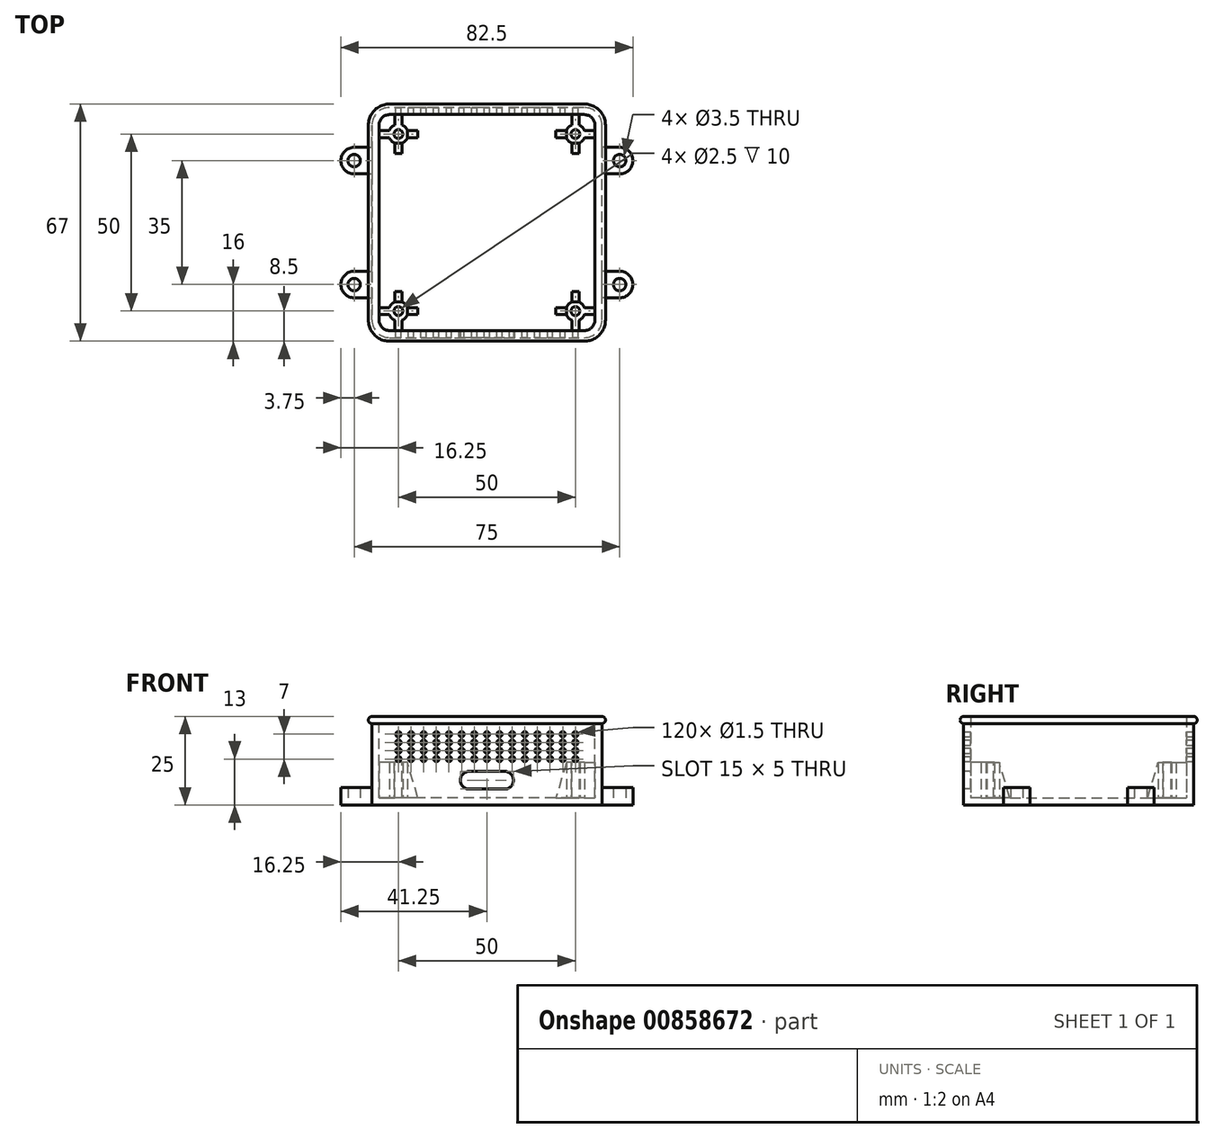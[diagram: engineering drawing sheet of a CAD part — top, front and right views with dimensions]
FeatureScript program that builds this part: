
annotation { "Feature Type Name" : "Feature", "Feature Type Description" : "" }
export const myFeature = defineFeature(function(context is Context, id is Id, definition is map)
    precondition{}
    {
        {
            var Q0;
            Q0=qCreatedBy(makeId("Top.planeOp"),FACE);
            var sketch = newSketch(context, id + "F0", { "sketchPlane" : qUnion([Q0])});
            skLineSegment(sketch, "E0.bottom", {"start": v(27.5, -32.5) * mm, "end": v(-27.5, -32.5) * mm});
            skLineSegment(sketch, "E0.top", {"start": v(27.5, 32.5) * mm, "end": v(-27.5, 32.5) * mm});
            skLineSegment(sketch, "E0.left", {"start": v(32.5, -27.5) * mm, "end": v(32.5, 27.5) * mm});
            skLineSegment(sketch, "E0.right", {"start": v(-32.5, -27.5) * mm, "end": v(-32.5, 27.5) * mm});
            skPoint(sketch, "E0.middle", {"position": v(0, 0) * mm});
            skPoint(sketch, "E1.visualSharp", {"position": v(-32.5, 32.5) * mm});
            skArc(sketch, "E1.filletArc", {"start": v(-27.5, 32.5) * mm, "mid": v(-31.04, 31.04) * mm, "end": v(-32.5, 27.5) * mm});
            skPoint(sketch, "E2.visualSharp", {"position": v(32.5, 32.5) * mm});
            skArc(sketch, "E2.filletArc", {"start": v(32.5, 27.5) * mm, "mid": v(31.04, 31.04) * mm, "end": v(27.5, 32.5) * mm});
            skPoint(sketch, "E3.visualSharp", {"position": v(32.5, -32.5) * mm});
            skArc(sketch, "E3.filletArc", {"start": v(27.5, -32.5) * mm, "mid": v(31.04, -31.04) * mm, "end": v(32.5, -27.5) * mm});
            skPoint(sketch, "E4.visualSharp", {"position": v(-32.5, -32.5) * mm});
            skArc(sketch, "E4.filletArc", {"start": v(-32.5, -27.5) * mm, "mid": v(-31.04, -31.04) * mm, "end": v(-27.5, -32.5) * mm});
            skSolve(sketch);
        }
        {
            var Q0;
            Q0 = qSketchRegion(id + "F0", true);
            extrude(context, id + "F1", {"entities" : qUnion([Q0]), "depth" : 25 * mm, "offsetDistance" : 25 * mm});
        }
        {
            var Q0;
            Q0=makeQuery(id+"F1.opExtrude","CAP_FACE",FACE,{"disambiguationData":[OSD([sQuery(id+"F0.wireOp",EDGE,"E0.bottom"),sQuery(id+"F0.wireOp",EDGE,"E0.top"),sQuery(id+"F0.wireOp",EDGE,"E0.left"),sQuery(id+"F0.wireOp",EDGE,"E0.right")])],"isStart":false});
            shell(context, id + "F2", {"entities" : qUnion([Q0]), "thickness" : 2 * mm});
        }
        {
            var Q0;
            Q0=qCreatedBy(makeId("Top.planeOp"),FACE);
            var sketch = newSketch(context, id + "F3", { "sketchPlane" : qUnion([Q0])});
            skLineSegment(sketch, "E5.bottom", {"start": v(-37.5, 21.25) * mm, "end": v(-32.5, 21.25) * mm});
            skLineSegment(sketch, "E5.top", {"start": v(-37.5, 13.75) * mm, "end": v(-32.5, 13.75) * mm});
            skLineSegment(sketch, "E5.right", {"start": v(-32.5, 21.25) * mm, "end": v(-32.5, 13.75) * mm});
            skArc(sketch, "E6", {"start": v(-37.5, 21.25) * mm, "mid": v(-41.25, 17.5) * mm, "end": v(-37.5, 13.75) * mm});
            skCircle(sketch, "E7", {"center": v(-37.5, 17.5) * mm, "radius": 1.75 * mm});
            skArc(sketch, "E8.MirrorCS", {"start": v(37.5, 21.25) * mm, "mid": v(41.25, 17.5) * mm, "end": v(37.5, 13.75) * mm});
            skCircle(sketch, "E9.MirrorC", {"center": v(37.5, 17.5) * mm, "radius": 1.75 * mm});
            skLineSegment(sketch, "E10.MirrorCS", {"start": v(32.5, 21.25) * mm, "end": v(32.5, 13.75) * mm});
            skLineSegment(sketch, "E11.MirrorCS", {"start": v(37.5, 13.75) * mm, "end": v(32.5, 13.75) * mm});
            skLineSegment(sketch, "E12.MirrorCS", {"start": v(37.5, 21.25) * mm, "end": v(32.5, 21.25) * mm});
            skLineSegment(sketch, "E13.MirrorCS", {"start": v(37.5, -13.75) * mm, "end": v(32.5, -13.75) * mm});
            skLineSegment(sketch, "E14.MirrorCS", {"start": v(-37.5, -13.75) * mm, "end": v(-32.5, -13.75) * mm});
            skCircle(sketch, "E15.MirrorC", {"center": v(-37.5, -17.5) * mm, "radius": 1.75 * mm});
            skArc(sketch, "E16.MirrorCS", {"start": v(-37.5, -21.25) * mm, "mid": v(-41.25, -17.5) * mm, "end": v(-37.5, -13.75) * mm});
            skLineSegment(sketch, "E17.MirrorCS", {"start": v(-32.5, -21.25) * mm, "end": v(-32.5, -13.75) * mm});
            skLineSegment(sketch, "E18.MirrorCS", {"start": v(37.5, -21.25) * mm, "end": v(32.5, -21.25) * mm});
            skArc(sketch, "E19.MirrorCS", {"start": v(37.5, -21.25) * mm, "mid": v(41.25, -17.5) * mm, "end": v(37.5, -13.75) * mm});
            skCircle(sketch, "E20.MirrorC", {"center": v(37.5, -17.5) * mm, "radius": 1.75 * mm});
            skLineSegment(sketch, "E21.MirrorCS", {"start": v(32.5, -21.25) * mm, "end": v(32.5, -13.75) * mm});
            skLineSegment(sketch, "E22.MirrorCS", {"start": v(-37.5, -21.25) * mm, "end": v(-32.5, -21.25) * mm});
            skSolve(sketch);
        }
        {
            var Q0;
            Q0 = qSketchRegion(id + "F3", true);
            extrude(context, id + "F4", {"entities" : qUnion([Q0]), "operationType" : NewBodyOperationType.ADD, "depth" : 5 * mm, "offsetDistance" : 25 * mm});
        }
        {
            var Q0;
            Q0=makeQuery(id+"F2.opShell","OFFSET_FACE",FACE,{"disambiguationData":[OSD([sQuery(id+"F0.wireOp",EDGE,"E0.bottom"),sQuery(id+"F0.wireOp",EDGE,"E0.top"),sQuery(id+"F0.wireOp",EDGE,"E0.left"),sQuery(id+"F0.wireOp",EDGE,"E0.right"),sQuery(id+"F0.wireOp",EDGE,"E1.filletArc"),sQuery(id+"F0.wireOp",EDGE,"E2.filletArc"),sQuery(id+"F0.wireOp",EDGE,"E3.filletArc"),sQuery(id+"F0.wireOp",EDGE,"E4.filletArc")])]});
            var sketch = newSketch(context, id + "F5", { "sketchPlane" : qUnion([Q0])});
            skLineSegment(sketch, "E23.bottom", {"start": v(-19.5, 24) * mm, "end": v(-22.44, 24) * mm});
            skLineSegment(sketch, "E23.top", {"start": v(-19.5, 26) * mm, "end": v(-22.44, 26) * mm});
            skLineSegment(sketch, "E23.left", {"start": v(-19.5, 24) * mm, "end": v(-19.5, 26) * mm});
            skLineSegment(sketch, "E23.right", {"start": v(-30.5, 24) * mm, "end": v(-30.5, 26) * mm});
            skPoint(sketch, "E23.middle", {"position": v(-25, 25) * mm});
            skLineSegment(sketch, "E24.bottom", {"start": v(-24, 19.5) * mm, "end": v(-26, 19.5) * mm});
            skLineSegment(sketch, "E24.top", {"start": v(-24, 30.5) * mm, "end": v(-26, 30.5) * mm});
            skLineSegment(sketch, "E24.left", {"start": v(-24, 19.5) * mm, "end": v(-24, 22.44) * mm});
            skLineSegment(sketch, "E24.right", {"start": v(-26, 19.5) * mm, "end": v(-26, 22.44) * mm});
            skArc(sketch, "E25", {"start": v(-26, 27.56) * mm, "mid": v(-26.94, 26.94) * mm, "end": v(-27.56, 26) * mm});
            skCircle(sketch, "E26", {"center": v(-25, 25) * mm, "radius": 1.25 * mm});
            skLineSegment(sketch, "E27.trimOffspring", {"start": v(-26, 27.56) * mm, "end": v(-26, 30.5) * mm});
            skLineSegment(sketch, "E28.trimOffspring", {"start": v(-27.56, 26) * mm, "end": v(-30.5, 26) * mm});
            skArc(sketch, "E29.trimOffspring", {"start": v(-27.56, 24) * mm, "mid": v(-26.94, 23.06) * mm, "end": v(-26, 22.44) * mm});
            skLineSegment(sketch, "E30.trimOffspring", {"start": v(-27.56, 24) * mm, "end": v(-30.5, 24) * mm});
            skLineSegment(sketch, "E31.trimOffspring", {"start": v(-24, 27.56) * mm, "end": v(-24, 30.5) * mm});
            skArc(sketch, "E32.trimOffspring", {"start": v(-22.44, 26) * mm, "mid": v(-23.06, 26.94) * mm, "end": v(-24, 27.56) * mm});
            skArc(sketch, "E33.trimOffspring", {"start": v(-24, 22.44) * mm, "mid": v(-23.06, 23.06) * mm, "end": v(-22.44, 24) * mm});
            skPoint(sketch, "E34.MirrorP", {"position": v(25, 25) * mm});
            skLineSegment(sketch, "E35.MirrorCS", {"start": v(24, 19.5) * mm, "end": v(26, 19.5) * mm});
            skArc(sketch, "E36.MirrorCS", {"start": v(26, 27.56) * mm, "mid": v(26.94, 26.94) * mm, "end": v(27.56, 26) * mm});
            skArc(sketch, "E37.MirrorCS", {"start": v(27.56, 24) * mm, "mid": v(26.94, 23.06) * mm, "end": v(26, 22.44) * mm});
            skLineSegment(sketch, "E38.MirrorCS", {"start": v(27.56, 24) * mm, "end": v(30.5, 24) * mm});
            skLineSegment(sketch, "E39.MirrorCS", {"start": v(19.5, 24) * mm, "end": v(22.44, 24) * mm});
            skLineSegment(sketch, "E40.MirrorCS", {"start": v(26, 27.56) * mm, "end": v(26, 30.5) * mm});
            skLineSegment(sketch, "E41.MirrorCS", {"start": v(27.56, 26) * mm, "end": v(30.5, 26) * mm});
            skLineSegment(sketch, "E42.MirrorCS", {"start": v(19.5, 26) * mm, "end": v(22.44, 26) * mm});
            skArc(sketch, "E43.MirrorCS", {"start": v(22.44, 26) * mm, "mid": v(23.06, 26.94) * mm, "end": v(24, 27.56) * mm});
            skLineSegment(sketch, "E44.MirrorCS", {"start": v(26, 19.5) * mm, "end": v(26, 22.44) * mm});
            skCircle(sketch, "E45.MirrorC", {"center": v(25, 25) * mm, "radius": 1.25 * mm});
            skLineSegment(sketch, "E46.MirrorCS", {"start": v(24, 27.56) * mm, "end": v(24, 30.5) * mm});
            skArc(sketch, "E47.MirrorCS", {"start": v(24, 22.44) * mm, "mid": v(23.06, 23.06) * mm, "end": v(22.44, 24) * mm});
            skLineSegment(sketch, "E48.MirrorCS", {"start": v(24, 30.5) * mm, "end": v(26, 30.5) * mm});
            skLineSegment(sketch, "E49.MirrorCS", {"start": v(19.5, 24) * mm, "end": v(19.5, 26) * mm});
            skLineSegment(sketch, "E50.MirrorCS", {"start": v(24, 19.5) * mm, "end": v(24, 22.44) * mm});
            skLineSegment(sketch, "E51.MirrorCS", {"start": v(30.5, 24) * mm, "end": v(30.5, 26) * mm});
            skArc(sketch, "E52.MirrorCS", {"start": v(26, -27.56) * mm, "mid": v(26.94, -26.94) * mm, "end": v(27.56, -26) * mm});
            skArc(sketch, "E53.MirrorCS", {"start": v(-24, -22.44) * mm, "mid": v(-23.06, -23.06) * mm, "end": v(-22.44, -24) * mm});
            skArc(sketch, "E54.MirrorCS", {"start": v(-22.44, -26) * mm, "mid": v(-23.06, -26.94) * mm, "end": v(-24, -27.56) * mm});
            skCircle(sketch, "E55.MirrorC", {"center": v(25, -25) * mm, "radius": 1.25 * mm});
            skArc(sketch, "E56.MirrorCS", {"start": v(27.56, -24) * mm, "mid": v(26.94, -23.06) * mm, "end": v(26, -22.44) * mm});
            skArc(sketch, "E57.MirrorCS", {"start": v(-27.56, -24) * mm, "mid": v(-26.94, -23.06) * mm, "end": v(-26, -22.44) * mm});
            skLineSegment(sketch, "E58.MirrorCS", {"start": v(19.5, -24) * mm, "end": v(19.5, -26) * mm});
            skLineSegment(sketch, "E59.MirrorCS", {"start": v(30.5, -24) * mm, "end": v(30.5, -26) * mm});
            skLineSegment(sketch, "E60.MirrorCS", {"start": v(-24, -30.5) * mm, "end": v(-26, -30.5) * mm});
            skArc(sketch, "E61.MirrorCS", {"start": v(-26, -27.56) * mm, "mid": v(-26.94, -26.94) * mm, "end": v(-27.56, -26) * mm});
            skArc(sketch, "E62.MirrorCS", {"start": v(24, -22.44) * mm, "mid": v(23.06, -23.06) * mm, "end": v(22.44, -24) * mm});
            skLineSegment(sketch, "E63.MirrorCS", {"start": v(24, -19.5) * mm, "end": v(26, -19.5) * mm});
            skCircle(sketch, "E64.MirrorC", {"center": v(-25, -25) * mm, "radius": 1.25 * mm});
            skLineSegment(sketch, "E65.MirrorCS", {"start": v(-24, -19.5) * mm, "end": v(-26, -19.5) * mm});
            skArc(sketch, "E66.MirrorCS", {"start": v(22.44, -26) * mm, "mid": v(23.06, -26.94) * mm, "end": v(24, -27.56) * mm});
            skLineSegment(sketch, "E67.MirrorCS", {"start": v(-19.5, -24) * mm, "end": v(-19.5, -26) * mm});
            skLineSegment(sketch, "E68.MirrorCS", {"start": v(-30.5, -24) * mm, "end": v(-30.5, -26) * mm});
            skLineSegment(sketch, "E69.MirrorCS", {"start": v(24, -30.5) * mm, "end": v(26, -30.5) * mm});
            skLineSegment(sketch, "E70.MirrorCS", {"start": v(-19.5, -26) * mm, "end": v(-22.44, -26) * mm});
            skLineSegment(sketch, "E71.MirrorCS", {"start": v(27.56, -24) * mm, "end": v(30.5, -24) * mm});
            skLineSegment(sketch, "E72.MirrorCS", {"start": v(27.56, -26) * mm, "end": v(30.5, -26) * mm});
            skLineSegment(sketch, "E73.MirrorCS", {"start": v(-24, -27.56) * mm, "end": v(-24, -30.5) * mm});
            skLineSegment(sketch, "E74.MirrorCS", {"start": v(24, -19.5) * mm, "end": v(24, -22.44) * mm});
            skLineSegment(sketch, "E75.MirrorCS", {"start": v(-26, -27.56) * mm, "end": v(-26, -30.5) * mm});
            skLineSegment(sketch, "E76.MirrorCS", {"start": v(26, -27.56) * mm, "end": v(26, -30.5) * mm});
            skLineSegment(sketch, "E77.MirrorCS", {"start": v(-27.56, -26) * mm, "end": v(-30.5, -26) * mm});
            skLineSegment(sketch, "E78.MirrorCS", {"start": v(19.5, -24) * mm, "end": v(22.44, -24) * mm});
            skLineSegment(sketch, "E79.MirrorCS", {"start": v(-19.5, -24) * mm, "end": v(-22.44, -24) * mm});
            skLineSegment(sketch, "E80.MirrorCS", {"start": v(-24, -19.5) * mm, "end": v(-24, -22.44) * mm});
            skLineSegment(sketch, "E81.MirrorCS", {"start": v(19.5, -26) * mm, "end": v(22.44, -26) * mm});
            skLineSegment(sketch, "E82.MirrorCS", {"start": v(24, -27.56) * mm, "end": v(24, -30.5) * mm});
            skLineSegment(sketch, "E83.MirrorCS", {"start": v(-26, -19.5) * mm, "end": v(-26, -22.44) * mm});
            skLineSegment(sketch, "E84.MirrorCS", {"start": v(-27.56, -24) * mm, "end": v(-30.5, -24) * mm});
            skLineSegment(sketch, "E85.MirrorCS", {"start": v(26, -19.5) * mm, "end": v(26, -22.44) * mm});
            skSolve(sketch);
        }
        {
            var Q0;
            Q0=makeQuery(id+"F5.imprint","IMPRINT",FACE,{"disambiguationData":[TD([[makeQuery(id+"F5.imprint","IMPRINT",EDGE,{"derivedFrom":sQuery(id+"F5.wireOp",EDGE,"E23.bottom")}),1.0]])]});
            cPlane(context, id + "F6", {"entities" : qUnion([Q0]), "cplaneType" : CPlaneType.OFFSET, "offset" : 10 * mm, "width" : 150 * mm, "height" : 150 * mm});
        }
        {
            var Q0;
            Q0 = qSketchRegion(id + "F5", true);
            extrude(context, id + "F7", {"entities" : qUnion([Q0]), "operationType" : NewBodyOperationType.ADD, "depth" : 10 * mm, "offsetDistance" : 25 * mm});
        }
        {
            var Q0;
            Q0=makeQuery(id+"F7.opExtrude","SWEPT_FACE",FACE,{"disambiguationData":[OSD([sQuery(id+"F5.wireOp",EDGE,"E23.top")])]});
            var sketch = newSketch(context, id + "F8", { "sketchPlane" : qUnion([Q0])});
            skLineSegment(sketch, "E86", {"start": v(19.5, 2) * mm, "end": v(19.5, 12) * mm});
            skLineSegment(sketch, "E87", {"start": v(19.5, 12) * mm, "end": v(22.44, 12) * mm});
            skLineSegment(sketch, "E88", {"start": v(22.44, 12) * mm, "end": v(19.5, 2) * mm});
            skLineSegment(sketch, "E89", {"start": v(-19.5, 12) * mm, "end": v(-22.44, 12) * mm});
            skLineSegment(sketch, "E90", {"start": v(-22.44, 12) * mm, "end": v(-19.5, 2) * mm});
            skLineSegment(sketch, "E91", {"start": v(-19.5, 2) * mm, "end": v(-19.5, 12) * mm});
            skSolve(sketch);
        }
        {
            var Q0;
            Q0 = qSketchRegion(id + "F8", true);
            var Q1;
            Q1=makeQuery(id+"F7.opExtrude","SWEPT_FACE",FACE,{"disambiguationData":[OSD([sQuery(id+"F5.wireOp",EDGE,"E70.MirrorCS")])]});
            extrude(context, id + "F9", {"entities" : qUnion([Q0]), "operationType" : NewBodyOperationType.REMOVE, "endBound" : BoundingType.UP_TO_SURFACE, "oppositeDirection" : true, "depth" : 25 * mm, "endBoundEntityFace" : qUnion([Q1]), "offsetDistance" : 25 * mm});
        }
        {
            var Q0;
            Q0=makeQuery(id+"F7.opExtrude","SWEPT_FACE",FACE,{"disambiguationData":[OSD([sQuery(id+"F5.wireOp",EDGE,"E24.right")])]});
            var sketch = newSketch(context, id + "F10", { "sketchPlane" : qUnion([Q0])});
            skLineSegment(sketch, "E92", {"start": v(-22.44, 12) * mm, "end": v(-19.5, 12) * mm});
            skLineSegment(sketch, "E93", {"start": v(-19.5, 12) * mm, "end": v(-19.5, 2) * mm});
            skLineSegment(sketch, "E94", {"start": v(-19.5, 2) * mm, "end": v(-22.44, 12) * mm});
            skLineSegment(sketch, "E95", {"start": v(19.5, 12) * mm, "end": v(22.44, 12) * mm});
            skLineSegment(sketch, "E96", {"start": v(19.5, 12) * mm, "end": v(19.5, 2) * mm});
            skLineSegment(sketch, "E97", {"start": v(19.5, 2) * mm, "end": v(22.44, 12) * mm});
            skSolve(sketch);
        }
        {
            var Q0;
            Q0 = qSketchRegion(id + "F10", true);
            var Q1;
            Q1=makeQuery(id+"F7.opExtrude","SWEPT_FACE",FACE,{"disambiguationData":[OSD([sQuery(id+"F5.wireOp",EDGE,"E44.MirrorCS")])]});
            extrude(context, id + "F11", {"entities" : qUnion([Q0]), "operationType" : NewBodyOperationType.REMOVE, "endBound" : BoundingType.UP_TO_SURFACE, "oppositeDirection" : true, "depth" : 25 * mm, "endBoundEntityFace" : qUnion([Q1]), "offsetDistance" : 25 * mm});
        }
        {
            var Q0;
            Q0=makeQuery(id+"F1.opExtrude","SWEPT_FACE",FACE,{"disambiguationData":[OSD([sQuery(id+"F0.wireOp",EDGE,"E0.bottom")])]});
            var sketch = newSketch(context, id + "F12", { "sketchPlane" : qUnion([Q0])});
            skLineSegment(sketch, "E98.bottom", {"start": v(5, 4.5) * mm, "end": v(-5, 4.5) * mm});
            skLineSegment(sketch, "E98.top", {"start": v(5, 9.5) * mm, "end": v(-5, 9.5) * mm});
            skPoint(sketch, "E98.middle.positionSnap0", {"position": v(0, 25) * mm});
            skPoint(sketch, "E98.centerSnap0", {"position": v(0, 25) * mm});
            skArc(sketch, "E99", {"start": v(-5, 9.5) * mm, "mid": v(-7.5, 7) * mm, "end": v(-5, 4.5) * mm});
            skArc(sketch, "E100", {"start": v(5, 9.5) * mm, "mid": v(7.5, 7) * mm, "end": v(5, 4.5) * mm});
            skSolve(sketch);
        }
        {
            var Q0;
            Q0 = qSketchRegion(id + "F12", true);
            extrude(context, id + "F13", {"entities" : qUnion([Q0]), "operationType" : NewBodyOperationType.REMOVE, "endBound" : BoundingType.UP_TO_NEXT, "oppositeDirection" : true, "depth" : 25 * mm, "offsetDistance" : 25 * mm});
        }
        {
            var Q0;
            Q0=makeQuery(id+"F1.opExtrude","SWEPT_FACE",FACE,{"disambiguationData":[OSD([sQuery(id+"F0.wireOp",EDGE,"E0.top")])]});
            var sketch = newSketch(context, id + "F14", { "sketchPlane" : qUnion([Q0])});
            skCircle(sketch, "E101", {"center": v(-25, 13) * mm, "radius": 0.75 * mm});
            skCircle(sketch, "E102.0.1.0", {"center": v(-25, 15.33) * mm, "radius": 0.75 * mm});
            skCircle(sketch, "E102.0.2.0", {"center": v(-25, 17.67) * mm, "radius": 0.75 * mm});
            skCircle(sketch, "E102.0.3.0", {"center": v(-25, 20) * mm, "radius": 0.75 * mm});
            skCircle(sketch, "E102.1.0.0", {"center": v(-21.43, 13) * mm, "radius": 0.75 * mm});
            skCircle(sketch, "E102.1.1.0", {"center": v(-21.43, 15.33) * mm, "radius": 0.75 * mm});
            skCircle(sketch, "E102.1.2.0", {"center": v(-21.43, 17.67) * mm, "radius": 0.75 * mm});
            skCircle(sketch, "E102.1.3.0", {"center": v(-21.43, 20) * mm, "radius": 0.75 * mm});
            skCircle(sketch, "E102.2.0.0", {"center": v(-17.86, 13) * mm, "radius": 0.75 * mm});
            skCircle(sketch, "E102.2.1.0", {"center": v(-17.86, 15.33) * mm, "radius": 0.75 * mm});
            skCircle(sketch, "E102.2.2.0", {"center": v(-17.86, 17.67) * mm, "radius": 0.75 * mm});
            skCircle(sketch, "E102.2.3.0", {"center": v(-17.86, 20) * mm, "radius": 0.75 * mm});
            skCircle(sketch, "E102.3.0.0", {"center": v(-14.29, 13) * mm, "radius": 0.75 * mm});
            skCircle(sketch, "E102.3.1.0", {"center": v(-14.29, 15.33) * mm, "radius": 0.75 * mm});
            skCircle(sketch, "E102.3.2.0", {"center": v(-14.29, 17.67) * mm, "radius": 0.75 * mm});
            skCircle(sketch, "E102.3.3.0", {"center": v(-14.29, 20) * mm, "radius": 0.75 * mm});
            skCircle(sketch, "E102.4.0.0", {"center": v(-10.71, 13) * mm, "radius": 0.75 * mm});
            skCircle(sketch, "E102.4.1.0", {"center": v(-10.71, 15.33) * mm, "radius": 0.75 * mm});
            skCircle(sketch, "E102.4.2.0", {"center": v(-10.71, 17.67) * mm, "radius": 0.75 * mm});
            skCircle(sketch, "E102.4.3.0", {"center": v(-10.71, 20) * mm, "radius": 0.75 * mm});
            skCircle(sketch, "E102.5.0.0", {"center": v(-7.14, 13) * mm, "radius": 0.75 * mm});
            skCircle(sketch, "E102.5.1.0", {"center": v(-7.14, 15.33) * mm, "radius": 0.75 * mm});
            skCircle(sketch, "E102.5.2.0", {"center": v(-7.14, 17.67) * mm, "radius": 0.75 * mm});
            skCircle(sketch, "E102.5.3.0", {"center": v(-7.14, 20) * mm, "radius": 0.75 * mm});
            skCircle(sketch, "E102.6.0.0", {"center": v(-3.57, 13) * mm, "radius": 0.75 * mm});
            skCircle(sketch, "E102.6.1.0", {"center": v(-3.57, 15.33) * mm, "radius": 0.75 * mm});
            skCircle(sketch, "E102.6.2.0", {"center": v(-3.57, 17.67) * mm, "radius": 0.75 * mm});
            skCircle(sketch, "E102.6.3.0", {"center": v(-3.57, 20) * mm, "radius": 0.75 * mm});
            skCircle(sketch, "E102.7.0.0", {"center": v(0, 13) * mm, "radius": 0.75 * mm});
            skCircle(sketch, "E102.7.1.0", {"center": v(0, 15.33) * mm, "radius": 0.75 * mm});
            skCircle(sketch, "E102.7.2.0", {"center": v(0, 17.67) * mm, "radius": 0.75 * mm});
            skCircle(sketch, "E102.7.3.0", {"center": v(0, 20) * mm, "radius": 0.75 * mm});
            skCircle(sketch, "E102.8.0.0", {"center": v(3.57, 13) * mm, "radius": 0.75 * mm});
            skCircle(sketch, "E102.8.1.0", {"center": v(3.57, 15.33) * mm, "radius": 0.75 * mm});
            skCircle(sketch, "E102.8.2.0", {"center": v(3.57, 17.67) * mm, "radius": 0.75 * mm});
            skCircle(sketch, "E102.8.3.0", {"center": v(3.57, 20) * mm, "radius": 0.75 * mm});
            skCircle(sketch, "E102.9.0.0", {"center": v(7.14, 13) * mm, "radius": 0.75 * mm});
            skCircle(sketch, "E102.9.1.0", {"center": v(7.14, 15.33) * mm, "radius": 0.75 * mm});
            skCircle(sketch, "E102.9.2.0", {"center": v(7.14, 17.67) * mm, "radius": 0.75 * mm});
            skCircle(sketch, "E102.9.3.0", {"center": v(7.14, 20) * mm, "radius": 0.75 * mm});
            skLineSegment(sketch, "E102.direction1", {"start": v(-25, 13) * mm, "end": v(-21.43, 13) * mm, "construction": true});
            skLineSegment(sketch, "E102.direction2", {"start": v(-25, 13) * mm, "end": v(-25, 15.33) * mm, "construction": true});
            skCircle(sketch, "E103.0.10.0", {"center": v(10.71, 13) * mm, "radius": 0.75 * mm});
            skCircle(sketch, "E103.0.10.1", {"center": v(10.71, 15.33) * mm, "radius": 0.75 * mm});
            skCircle(sketch, "E103.0.10.2", {"center": v(10.71, 17.67) * mm, "radius": 0.75 * mm});
            skCircle(sketch, "E103.0.10.3", {"center": v(10.71, 20) * mm, "radius": 0.75 * mm});
            skCircle(sketch, "E103.0.11.0", {"center": v(14.29, 13) * mm, "radius": 0.75 * mm});
            skCircle(sketch, "E103.0.11.1", {"center": v(14.29, 15.33) * mm, "radius": 0.75 * mm});
            skCircle(sketch, "E103.0.11.2", {"center": v(14.29, 17.67) * mm, "radius": 0.75 * mm});
            skCircle(sketch, "E103.0.11.3", {"center": v(14.29, 20) * mm, "radius": 0.75 * mm});
            skCircle(sketch, "E103.0.12.0", {"center": v(17.86, 13) * mm, "radius": 0.75 * mm});
            skCircle(sketch, "E103.0.12.1", {"center": v(17.86, 15.33) * mm, "radius": 0.75 * mm});
            skCircle(sketch, "E103.0.12.2", {"center": v(17.86, 17.67) * mm, "radius": 0.75 * mm});
            skCircle(sketch, "E103.0.12.3", {"center": v(17.86, 20) * mm, "radius": 0.75 * mm});
            skCircle(sketch, "E103.0.13.0", {"center": v(21.43, 13) * mm, "radius": 0.75 * mm});
            skCircle(sketch, "E103.0.13.1", {"center": v(21.43, 15.33) * mm, "radius": 0.75 * mm});
            skCircle(sketch, "E103.0.13.2", {"center": v(21.43, 17.67) * mm, "radius": 0.75 * mm});
            skCircle(sketch, "E103.0.13.3", {"center": v(21.43, 20) * mm, "radius": 0.75 * mm});
            skCircle(sketch, "E103.0.14.0", {"center": v(25, 13) * mm, "radius": 0.75 * mm});
            skCircle(sketch, "E103.0.14.1", {"center": v(25, 15.33) * mm, "radius": 0.75 * mm});
            skCircle(sketch, "E103.0.14.2", {"center": v(25, 17.67) * mm, "radius": 0.75 * mm});
            skCircle(sketch, "E103.0.14.3", {"center": v(25, 20) * mm, "radius": 0.75 * mm});
            skSolve(sketch);
        }
        {
            var Q0;
            Q0 = qSketchRegion(id + "F14", true);
            var Q1;
            Q1=makeQuery(id+"F1.opExtrude","SWEPT_FACE",FACE,{"disambiguationData":[OSD([sQuery(id+"F0.wireOp",EDGE,"E0.bottom")])]});
            extrude(context, id + "F15", {"entities" : qUnion([Q0]), "operationType" : NewBodyOperationType.REMOVE, "endBound" : BoundingType.UP_TO_SURFACE, "oppositeDirection" : true, "depth" : 25 * mm, "endBoundEntityFace" : qUnion([Q1]), "offsetDistance" : 25 * mm});
        }
        {
            var Q0;
            Q0=qCreatedBy(makeId("Right.planeOp"),FACE);
            var sketch = newSketch(context, id + "F16", { "sketchPlane" : qUnion([Q0])});
            skArc(sketch, "E104", {"start": v(-32.5, 25) * mm, "mid": v(-33.5, 24) * mm, "end": v(-32.5, 23) * mm});
            skLineSegment(sketch, "E105", {"start": v(-32.5, 25) * mm, "end": v(-32.5, 23) * mm});
            skSolve(sketch);
        }
        {
            var Q0;
            Q0=makeQuery(id+"F16.imprint","IMPRINT",FACE,{"disambiguationData":[TD([[makeQuery(id+"F16.imprint","IMPRINT",EDGE,{"derivedFrom":sQuery(id+"F16.wireOp",EDGE,"E104")}),1.0]])]});
            var Q1;
            Q1=makeQuery(id+"F1.opExtrude","CAP_EDGE",EDGE,{"disambiguationData":[OSD([sQuery(id+"F0.wireOp",EDGE,"E0.bottom")])],"isStart":false});
            var Q2;
            Q2=makeQuery(id+"F1.opExtrude","CAP_EDGE",EDGE,{"disambiguationData":[OSD([sQuery(id+"F0.wireOp",EDGE,"E4.filletArc")])],"isStart":false});
            var Q3;
            Q3=makeQuery(id+"F1.opExtrude","CAP_EDGE",EDGE,{"disambiguationData":[OSD([sQuery(id+"F0.wireOp",EDGE,"E0.right")])],"isStart":false});
            var Q4;
            Q4=makeQuery(id+"F1.opExtrude","CAP_EDGE",EDGE,{"disambiguationData":[OSD([sQuery(id+"F0.wireOp",EDGE,"E1.filletArc")])],"isStart":false});
            var Q5;
            Q5=makeQuery(id+"F1.opExtrude","CAP_EDGE",EDGE,{"disambiguationData":[OSD([sQuery(id+"F0.wireOp",EDGE,"E0.top")])],"isStart":false});
            var Q6;
            Q6=makeQuery(id+"F1.opExtrude","CAP_EDGE",EDGE,{"disambiguationData":[OSD([sQuery(id+"F0.wireOp",EDGE,"E2.filletArc")])],"isStart":false});
            var Q7;
            Q7=makeQuery(id+"F1.opExtrude","CAP_EDGE",EDGE,{"disambiguationData":[OSD([sQuery(id+"F0.wireOp",EDGE,"E0.left")])],"isStart":false});
            var Q8;
            Q8=makeQuery(id+"F1.opExtrude","CAP_EDGE",EDGE,{"disambiguationData":[OSD([sQuery(id+"F0.wireOp",EDGE,"E3.filletArc")])],"isStart":false});
            sweep(context, id + "F17", {"operationType" : NewBodyOperationType.ADD, "profiles" : qUnion([Q0]), "path" : qUnion([Q1, Q2, Q3, Q4, Q5, Q6, Q7, Q8])});
        }
    });
